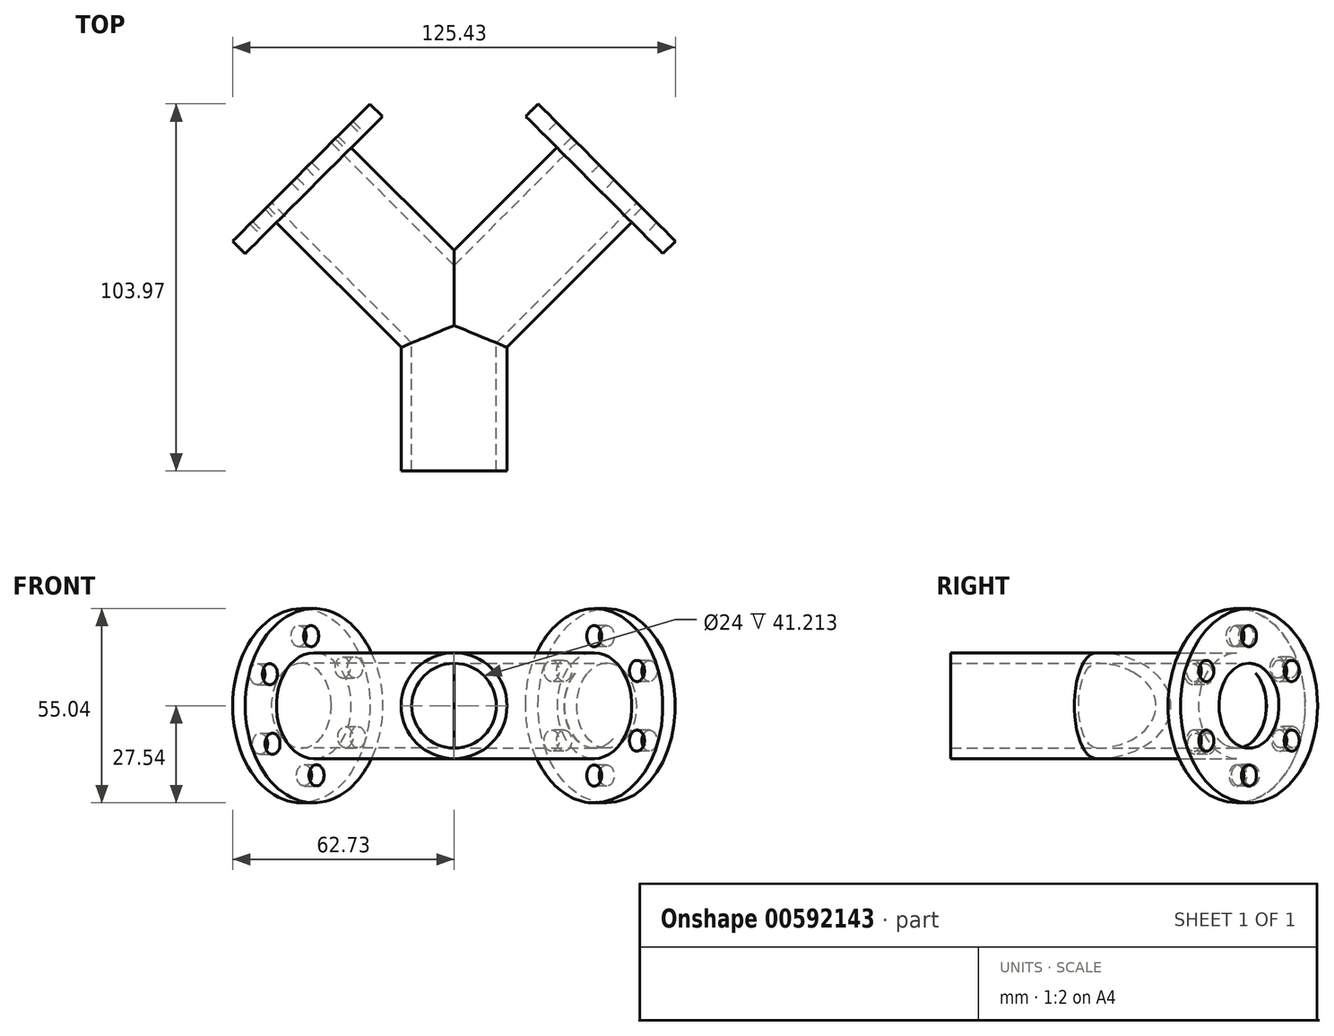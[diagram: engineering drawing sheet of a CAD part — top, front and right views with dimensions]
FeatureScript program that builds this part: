
annotation { "Feature Type Name" : "Feature", "Feature Type Description" : "" }
export const myFeature = defineFeature(function(context is Context, id is Id, definition is map)
    precondition{}
    {
        {
            var Q0;
            Q0=qCreatedBy(makeId("Front.planeOp"),FACE);
            var sketch = newSketch(context, id + "F0", { "sketchPlane" : qUnion([Q0])});
            skCircle(sketch, "E0", {"center": v(0, 0) * mm, "radius": 15 * mm});
            skSolve(sketch);
        }
        {
            var Q0;
            Q0=qCreatedBy(makeId("Top.planeOp"),FACE);
            var sketch = newSketch(context, id + "F1", { "sketchPlane" : qUnion([Q0])});
            skLineSegment(sketch, "E1", {"start": v(0, 0) * mm, "end": v(0, 36.21) * mm});
            skLineSegment(sketch, "E2", {"start": v(0, 36.21) * mm, "end": v(39.75, 75.96) * mm});
            skLineSegment(sketch, "E3", {"start": v(0, 36.21) * mm, "end": v(-39.75, 75.96) * mm});
            skLineSegment(sketch, "E4.0", {"start": v(-15, 30) * mm, "end": v(-50.36, 65.36) * mm});
            skLineSegment(sketch, "E4.1", {"start": v(-15, 0) * mm, "end": v(-15, 30) * mm});
            skLineSegment(sketch, "E5.0", {"start": v(15, 30) * mm, "end": v(50.36, 65.36) * mm});
            skLineSegment(sketch, "E5.1", {"start": v(15, 0) * mm, "end": v(15, 30) * mm});
            skLineSegment(sketch, "E6", {"start": v(50.36, 65.36) * mm, "end": v(35.4, 80.3) * mm});
            skSolve(sketch);
        }
        {
            var Q0;
            Q0=makeQuery(id+"F0.imprint","IMPRINT",FACE,{"disambiguationData":[TD([[makeQuery(id+"F0.imprint","IMPRINT",EDGE,{"derivedFrom":sQuery(id+"F0.wireOp",EDGE,"E0")}),1.0]])]});
            var Q1;
            Q1=sQuery(id+"F1.wireOp",EDGE,"E2");
            var Q2;
            Q2=sQuery(id+"F1.wireOp",EDGE,"E1");
            sweep(context, id + "F2", {"profiles" : qUnion([Q0]), "path" : qUnion([Q1, Q2])});
        }
        {
            var Q0;
            Q0=makeQuery(id+"F2.opSweep","CAP_FACE",FACE,{"disambiguationData":[OSD([sQuery(id+"F0.wireOp",EDGE,"E0"),sQuery(id+"F1.wireOp",VERTEX,"E1.start")])],"isStart":true});
            var Q1;
            Q1=sQuery(id+"F1.wireOp",EDGE,"E1");
            var Q2;
            Q2=sQuery(id+"F1.wireOp",EDGE,"E3");
            sweep(context, id + "F3", {"operationType" : NewBodyOperationType.ADD, "profiles" : qUnion([Q0]), "path" : qUnion([Q1, Q2])});
        }
        {
            var Q0;
            Q0=makeQuery(id+"F3.opSweep","CAP_FACE",FACE,{"disambiguationData":[OSD([sQuery(id+"F0.wireOp",EDGE,"E0"),sQuery(id+"F1.wireOp",VERTEX,"E1.start"),sQuery(id+"F1.wireOp",VERTEX,"E3.end")])],"isStart":false});
            var Q1;
            Q1=makeQuery(id+"F2.opSweep","CAP_FACE",FACE,{"disambiguationData":[OSD([sQuery(id+"F0.wireOp",EDGE,"E0"),sQuery(id+"F1.wireOp",VERTEX,"E2.end")])],"isStart":false});
            var Q2;
            Q2=makeQuery(id+"F2.opSweep","CAP_FACE",FACE,{"disambiguationData":[OSD([sQuery(id+"F0.wireOp",EDGE,"E0"),sQuery(id+"F1.wireOp",VERTEX,"E1.start")])],"isStart":true});
            shell(context, id + "F4", {"entities" : qUnion([Q0, Q1, Q2]), "thickness" : 3 * mm});
        }
        {
            var Q0;
            Q0=qCreatedBy(makeId("Front.planeOp"),FACE);
            var sketch = newSketch(context, id + "F5", { "sketchPlane" : qUnion([Q0])});
            skCircle(sketch, "E7", {"center": v(0, 0) * mm, "radius": 12 * mm});
            skCircle(sketch, "E8", {"center": v(0, 0) * mm, "radius": 27.5 * mm});
            skCircle(sketch, "E9", {"center": v(0, 0) * mm, "radius": 19.75 * mm, "construction": true});
            skCircle(sketch, "E10", {"center": v(0, 19.75) * mm, "radius": 3 * mm});
            skCircle(sketch, "E11.1.0", {"center": v(-17.1, 9.88) * mm, "radius": 3 * mm});
            skCircle(sketch, "E11.2.0", {"center": v(-17.1, -9.87) * mm, "radius": 3 * mm});
            skCircle(sketch, "E11.3.0", {"center": v(0, -19.75) * mm, "radius": 3 * mm});
            skCircle(sketch, "E11.4.0", {"center": v(17.1, -9.88) * mm, "radius": 3 * mm});
            skCircle(sketch, "E11.5.0", {"center": v(17.1, 9.88) * mm, "radius": 3 * mm});
            skCircle(sketch, "E12.0", {"center": v(0, 0) * mm, "radius": 15 * mm});
            skSolve(sketch);
        }
        {
            var Q0;
            Q0=makeQuery(id+"F5.imprint","IMPRINT",FACE,{"disambiguationData":[TD([[makeQuery(id+"F5.imprint","IMPRINT",EDGE,{"derivedFrom":sQuery(id+"F5.wireOp",EDGE,"E7")}),-1.0]])]});
            extrude(context, id + "F6", {"entities" : qUnion([Q0]), "operationType" : NewBodyOperationType.ADD, "depth" : 5 * mm, "offsetDistance" : 25 * mm});
        }
        {
            var Q0;
            Q0=makeQuery(id+"F3.opSweep","CAP_FACE",FACE,{"disambiguationData":[OSD([sQuery(id+"F0.wireOp",EDGE,"E0"),sQuery(id+"F1.wireOp",VERTEX,"E1.start"),sQuery(id+"F1.wireOp",VERTEX,"E3.end")])],"isStart":false});
            var sketch = newSketch(context, id + "F7", { "sketchPlane" : qUnion([Q0])});
            skCircle(sketch, "E13", {"center": v(-25.6, 0) * mm, "radius": 12 * mm});
            skCircle(sketch, "E14", {"center": v(-25.6, 0) * mm, "radius": 27.5 * mm});
            skCircle(sketch, "E15", {"center": v(-25.6, 0) * mm, "radius": 19.75 * mm, "construction": true});
            skCircle(sketch, "E16", {"center": v(-24.53, 19.72) * mm, "radius": 3 * mm});
            skCircle(sketch, "E17.1.0", {"center": v(-42.15, 10.8) * mm, "radius": 3 * mm});
            skCircle(sketch, "E17.2.0", {"center": v(-43.22, -8.93) * mm, "radius": 3 * mm});
            skCircle(sketch, "E17.3.0", {"center": v(-26.69, -19.72) * mm, "radius": 3 * mm});
            skCircle(sketch, "E17.4.0", {"center": v(-9.07, -10.8) * mm, "radius": 3 * mm});
            skCircle(sketch, "E17.5.0", {"center": v(-7.99, 8.93) * mm, "radius": 3 * mm});
            skSolve(sketch);
        }
        {
            var Q0;
            Q0=makeQuery(id+"F7.imprint","IMPRINT",FACE,{"disambiguationData":[TD([[makeQuery(id+"F7.imprint","IMPRINT",EDGE,{"derivedFrom":sQuery(id+"F7.wireOp",EDGE,"E14")}),1.0]])]});
            var Q1;
            {var subQ0=sQuery(id+"F1.wireOp",VERTEX,"E3.end");var subQ1=sQuery(id+"F1.wireOp",VERTEX,"E1.start");var subQ2=sQuery(id+"F0.wireOp",EDGE,"E0");Q1=makeQuery(id+"F7.imprint","IMPRINT",FACE,{"disambiguationData":[TD([[makeQuery(id+"F7.imprint","IMPRINT",EDGE,{"derivedFrom":makeQuery(id+"F3.opSweep","CAP_EDGE",EDGE,{"disambiguationData":[OSD([subQ2,subQ1,subQ0])],"isStart":false})}),1.0]])]});}
            extrude(context, id + "F8", {"entities" : qUnion([Q0, Q1]), "operationType" : NewBodyOperationType.ADD, "depth" : 5 * mm, "offsetDistance" : 25 * mm});
        }
        {
            var Q0;
            Q0=makeQuery(id+"F2.opSweep","CAP_FACE",FACE,{"disambiguationData":[OSD([sQuery(id+"F0.wireOp",EDGE,"E0"),sQuery(id+"F1.wireOp",VERTEX,"E2.end")])],"isStart":false});
            var sketch = newSketch(context, id + "F9", { "sketchPlane" : qUnion([Q0])});
            skPoint(sketch, "E18", {"position": v(25.6, 0) * mm});
            skCircle(sketch, "E19", {"center": v(25.65, -0.04) * mm, "radius": 12 * mm});
            skCircle(sketch, "E20", {"center": v(25.65, -0.04) * mm, "radius": 27.5 * mm});
            skCircle(sketch, "E21", {"center": v(25.65, -0.04) * mm, "radius": 19.75 * mm, "construction": true});
            skCircle(sketch, "E22", {"center": v(25.65, 19.71) * mm, "radius": 3 * mm});
            skCircle(sketch, "E23.1.0", {"center": v(8.54, 9.84) * mm, "radius": 3 * mm});
            skCircle(sketch, "E23.2.0", {"center": v(8.54, -9.91) * mm, "radius": 3 * mm});
            skCircle(sketch, "E23.3.0", {"center": v(25.65, -19.79) * mm, "radius": 3 * mm});
            skCircle(sketch, "E23.4.0", {"center": v(42.75, -9.91) * mm, "radius": 3 * mm});
            skCircle(sketch, "E23.5.0", {"center": v(42.75, 9.84) * mm, "radius": 3 * mm});
            skSolve(sketch);
        }
        {
            var Q0;
            {var subQ0=sQuery(id+"F1.wireOp",VERTEX,"E2.end");var subQ1=sQuery(id+"F0.wireOp",EDGE,"E0");Q0=makeQuery(id+"F9.imprint","IMPRINT",FACE,{"disambiguationData":[TD([[makeQuery(id+"F9.imprint","IMPRINT",EDGE,{"derivedFrom":makeQuery(id+"F2.opSweep","CAP_EDGE",EDGE,{"disambiguationData":[OSD([subQ1,subQ0])],"isStart":false})}),1.0]])]});}
            var Q1;
            Q1=makeQuery(id+"F9.imprint","IMPRINT",FACE,{"disambiguationData":[TD([[makeQuery(id+"F9.imprint","IMPRINT",EDGE,{"derivedFrom":sQuery(id+"F9.wireOp",EDGE,"E20")}),1.0]])]});
            extrude(context, id + "F10", {"entities" : qUnion([Q0, Q1]), "operationType" : NewBodyOperationType.ADD, "depth" : 5 * mm, "offsetDistance" : 25 * mm});
        }
    });
